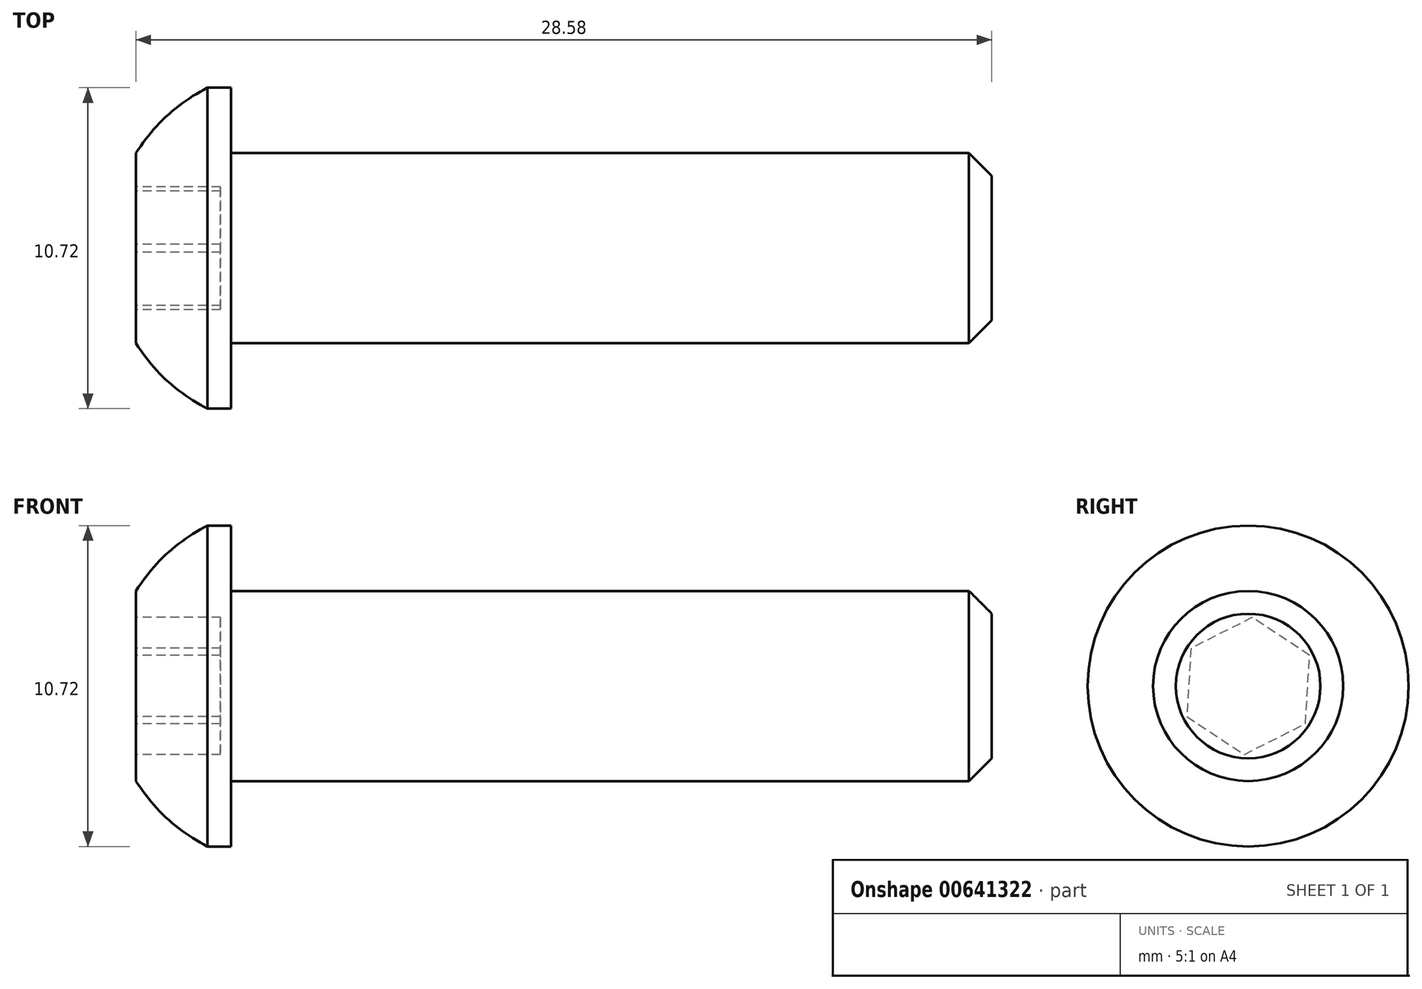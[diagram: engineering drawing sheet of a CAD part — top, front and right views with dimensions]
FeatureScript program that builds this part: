
annotation { "Feature Type Name" : "Feature", "Feature Type Description" : "" }
export const myFeature = defineFeature(function(context is Context, id is Id, definition is map)
    precondition{}
    {
        {
            var Q0;
            Q0=qCreatedBy(makeId("Front.planeOp"),FACE);
            var sketch = newSketch(context, id + "F0", { "sketchPlane" : qUnion([Q0])});
            skLineSegment(sketch, "E0", {"start": v(0, 0) * mm, "end": v(25.4, 0) * mm});
            skLineSegment(sketch, "E1", {"start": v(0, 0) * mm, "end": v(0, 5.36) * mm});
            skLineSegment(sketch, "E2", {"start": v(0, 5.36) * mm, "end": v(-0.79, 5.36) * mm});
            skLineSegment(sketch, "E3", {"start": v(0, 0) * mm, "end": v(-3.18, 0) * mm});
            skLineSegment(sketch, "E4", {"start": v(-3.18, 0) * mm, "end": v(-3.18, 3.18) * mm});
            skLineSegment(sketch, "E5.MirrorCS", {"start": v(0, 3.18) * mm, "end": v(25.4, 3.18) * mm});
            skLineSegment(sketch, "E6", {"start": v(25.4, 0) * mm, "end": v(25.4, 3.18) * mm});
            skArc(sketch, "E7", {"start": v(-0.79, 5.36) * mm, "mid": v(-2.13, 4.43) * mm, "end": v(-3.18, 3.17) * mm});
            skSolve(sketch);
        }
        {
            var Q0;
            Q0 = qSketchRegion(id + "F0", true);
            var Q1;
            Q1=sQuery(id+"F0.wireOp",EDGE,"E0");
            revolve(context, id + "F1", {"entities" : qUnion([Q0]), "axis" : qUnion([Q1]), "revolveType" : RevolveType.FULL});
        }
        {
            var Q0;
            Q0=makeQuery(id+"F1.opRevolve","SWEPT_FACE",FACE,{"disambiguationData":[OSD([sQuery(id+"F0.wireOp",EDGE,"E4")])]});
            var sketch = newSketch(context, id + "F2", { "sketchPlane" : qUnion([Q0])});
            skPoint(sketch, "E8.0", {"position": v(0, 0) * mm});
            skLineSegment(sketch, "E9.0", {"start": v(-0.14, 2.29) * mm, "end": v(1.91, 1.26) * mm});
            skLineSegment(sketch, "E9.1", {"start": v(1.91, 1.26) * mm, "end": v(2.05, -1.02) * mm});
            skLineSegment(sketch, "E9.2", {"start": v(2.05, -1.02) * mm, "end": v(0.14, -2.29) * mm});
            skLineSegment(sketch, "E9.3", {"start": v(0.14, -2.29) * mm, "end": v(-1.91, -1.26) * mm});
            skLineSegment(sketch, "E9.4", {"start": v(-1.91, -1.26) * mm, "end": v(-2.05, 1.02) * mm});
            skLineSegment(sketch, "E9.5", {"start": v(-2.05, 1.02) * mm, "end": v(-0.14, 2.29) * mm});
            skPoint(sketch, "E9.0.midPoint", {"position": v(0.89, 1.77) * mm});
            skSolve(sketch);
        }
        {
            var Q0;
            {var subQ0=sQuery(id+"F2.wireOp",EDGE,"ehG4KJab-ZW6D-AEX6-JAdQ-D1GuambJplyh");var subQ4=makeQuery(id+"F2.imprint","INTERSECT",VERTEX,{"derivedFrom":[subQ0,sQuery(id+"F2.wireOp",EDGE,"E9.0")]});Q0=makeQuery(id+"F2.imprint","IMPRINT",FACE,{"disambiguationData":[TD([[makeQuery(id+"F2.imprint","IMPRINT",EDGE,{"disambiguationData":[TD([[subQ4,1.0]])],"derivedFrom":subQ0}),1.0]])]});}
            var Q1;
            Q1=makeQuery(id+"F2.imprint","IMPRINT",FACE,{"disambiguationData":[TD([[makeQuery(id+"F2.imprint","IMPRINT",EDGE,{"derivedFrom":sQuery(id+"F2.wireOp",EDGE,"E9.0")}),-1.0]])]});
            extrude(context, id + "F3", {"entities" : qUnion([Q0, Q1]), "operationType" : NewBodyOperationType.REMOVE, "oppositeDirection" : true, "depth" : 2.82 * mm, "offsetDistance" : 25.4 * mm});
        }
        {
            var Q0;
            Q0=makeQuery(id+"F1.opRevolve","SWEPT_FACE",FACE,{"disambiguationData":[OSD([sQuery(id+"F0.wireOp",EDGE,"E6")])]});
            chamfer(context, id + "F4", {"entities" : qUnion([Q0]), "chamferType" : ChamferType.OFFSET_ANGLE, "width" : 0.76 * mm, "oppositeDirection" : false, "angle" : 45 * degree, "tangentPropagation" : true});
        }
    });
